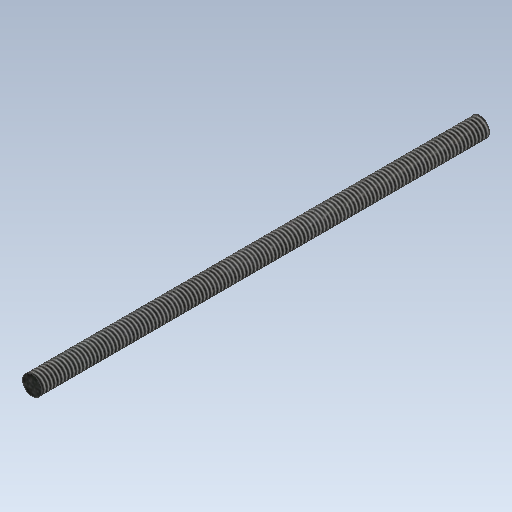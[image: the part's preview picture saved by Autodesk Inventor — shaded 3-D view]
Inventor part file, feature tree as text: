
AUTODESK INVENTOR PART (.ipt)
format: ipt  version: 2020 (Build 240168000, 168)  size: 115,200 bytes
history: native  units: mm
features: extrude x1, thread x1, sketch x1
ambient origin geometry x8: Origin, YZ Plane, XZ Plane, XY Plane, X Axis, Y Axis, Z Axis, Center Point
bodies: Solid1 (feature_tree)
feature tree (3):
  extrude  "Extrusion1"  Depth=185.0mm TaperAngle=0.0deg
  thread  "Thread1"  [1 undecoded]
  sketch  "Sketch1"  dims[d0=8.0mm d1=185.0mm d2=0.0mm d3=200.0mm d4=0.0mm]
note: 1 required parameter value undecoded (feature->parameter linkage not recoverable at this tier; creation-order binding heuristic only, values carry confidence <= 0.55)
